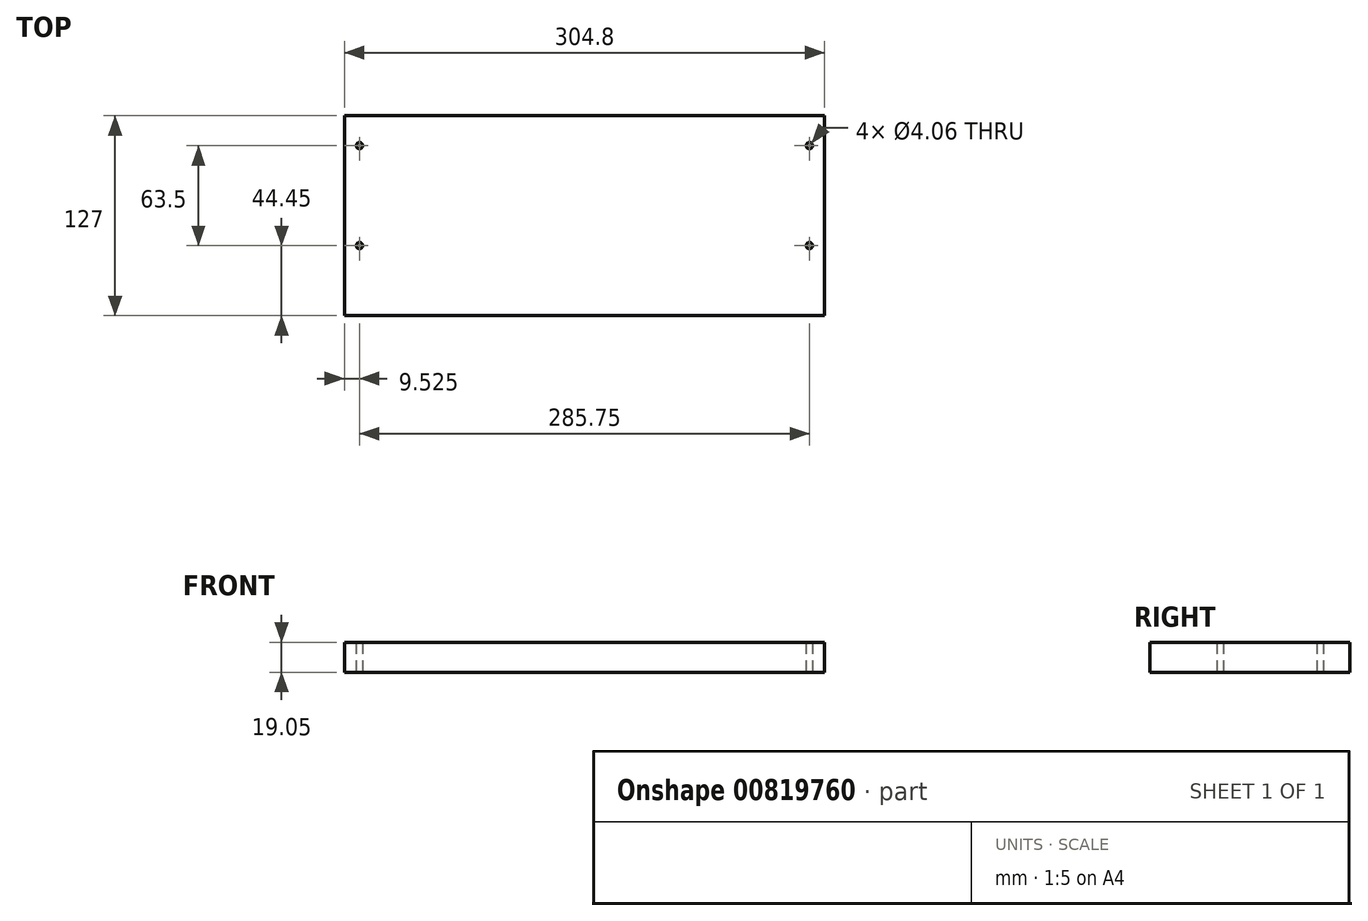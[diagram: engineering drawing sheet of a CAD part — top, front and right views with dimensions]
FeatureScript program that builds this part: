
annotation { "Feature Type Name" : "Feature", "Feature Type Description" : "" }
export const myFeature = defineFeature(function(context is Context, id is Id, definition is map)
    precondition{}
    {
        {
            var Q0;
            Q0=qCreatedBy(makeId("Top.planeOp"),FACE);
            var sketch = newSketch(context, id + "F0", { "sketchPlane" : qUnion([Q0])});
            skLineSegment(sketch, "E0.bottom", {"start": v(-152.4, 63.5) * mm, "end": v(152.4, 63.5) * mm});
            skLineSegment(sketch, "E0.top", {"start": v(-152.4, -63.5) * mm, "end": v(152.4, -63.5) * mm});
            skLineSegment(sketch, "E0.left", {"start": v(-152.4, 63.5) * mm, "end": v(-152.4, -63.5) * mm});
            skLineSegment(sketch, "E0.right", {"start": v(152.4, 63.5) * mm, "end": v(152.4, -63.5) * mm});
            skPoint(sketch, "E0.middle", {"position": v(0, 0) * mm});
            skLineSegment(sketch, "E1", {"start": v(-142.88, 63.5) * mm, "end": v(-142.88, -63.5) * mm, "construction": true});
            skLineSegment(sketch, "E2", {"start": v(142.88, 63.5) * mm, "end": v(142.88, -63.5) * mm, "construction": true});
            skLineSegment(sketch, "E3", {"start": v(152.4, 44.45) * mm, "end": v(-152.4, 44.45) * mm, "construction": true});
            skLineSegment(sketch, "E4", {"start": v(-152.4, -19.05) * mm, "end": v(152.4, -19.05) * mm, "construction": true});
            skCircle(sketch, "E5", {"center": v(-142.88, 44.45) * mm, "radius": 2.03 * mm});
            skCircle(sketch, "E6", {"center": v(-142.88, -19.05) * mm, "radius": 2.03 * mm});
            skCircle(sketch, "E7", {"center": v(142.88, -19.05) * mm, "radius": 2.03 * mm});
            skCircle(sketch, "E8", {"center": v(142.88, 44.45) * mm, "radius": 2.03 * mm});
            skSolve(sketch);
        }
        {
            var Q0;
            Q0=makeQuery(id+"F0.imprint","IMPRINT",FACE,{"disambiguationData":[TD([[makeQuery(id+"F0.imprint","IMPRINT",EDGE,{"derivedFrom":sQuery(id+"F0.wireOp",EDGE,"E0.bottom")}),-1.0]])]});
            extrude(context, id + "F1", {"entities" : qUnion([Q0]), "depth" : 19.05 * mm, "offsetDistance" : 25.4 * mm});
        }
    });
